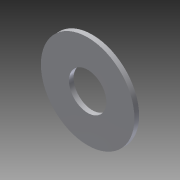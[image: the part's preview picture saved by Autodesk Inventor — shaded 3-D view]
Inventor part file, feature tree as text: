
AUTODESK INVENTOR PART (.ipt)
format: ipt  version: 2013 (Build 170138000, 138)  size: 75,264 bytes
history: native  units: mm
features: other x1, extrude x1, sketch x1
ambient origin geometry x8: Origin, YZ Plane, XZ Plane, XY Plane, X Axis, Y Axis, Z Axis, Center Point
feature tree (3):
  other  "ソリッド1"
  extrude  "押し出し1"  Depth=20.0mm
  sketch  "スケッチ1"
